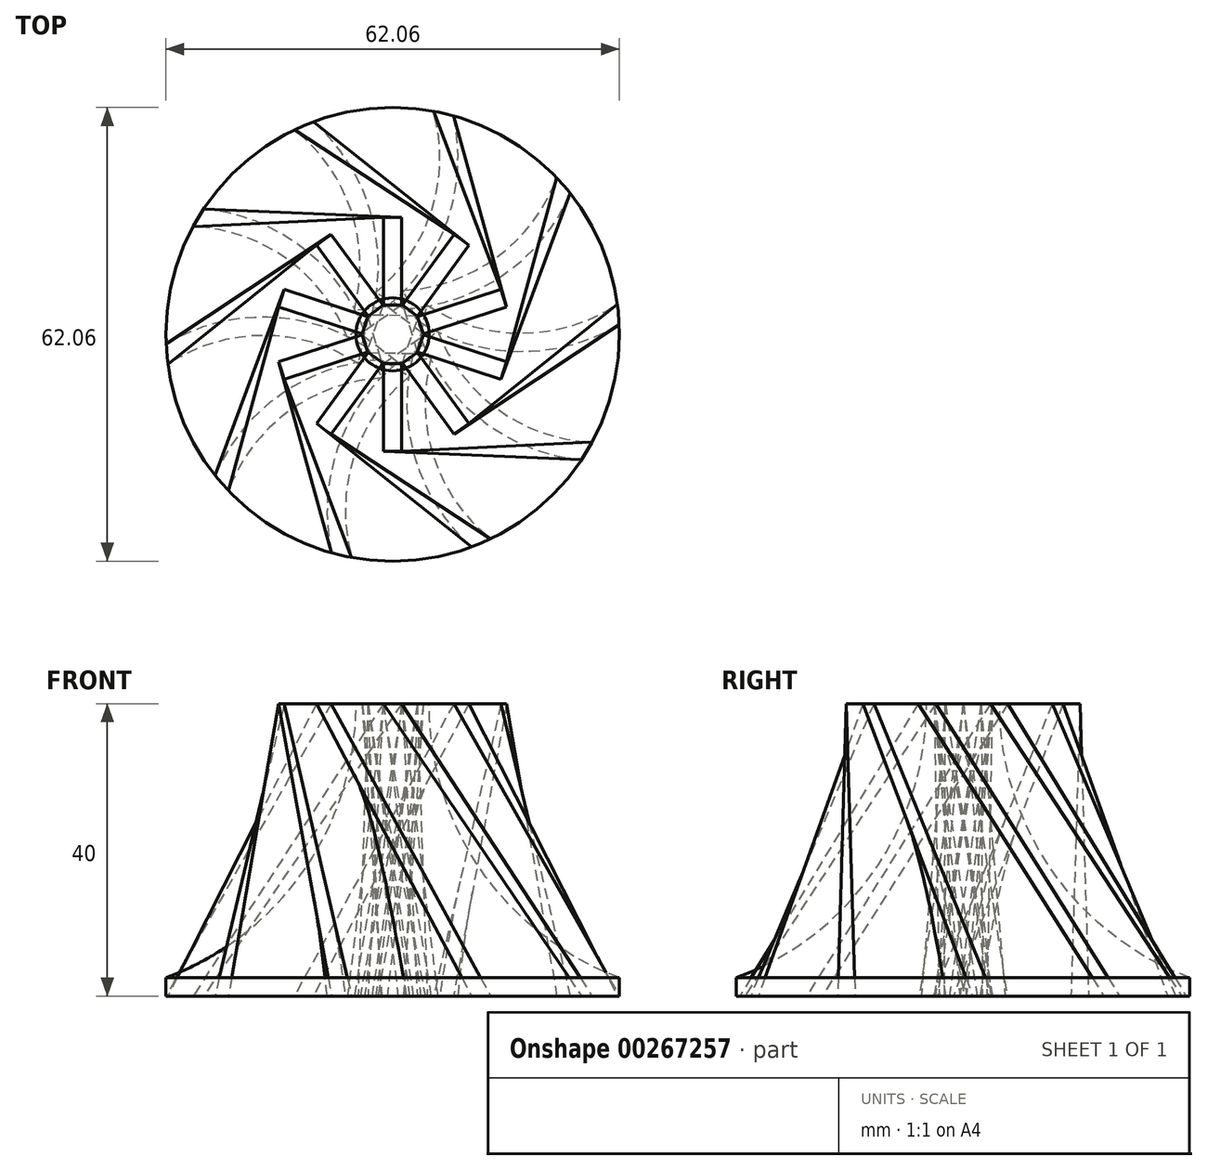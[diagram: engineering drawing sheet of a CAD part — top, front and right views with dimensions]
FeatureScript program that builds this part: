
annotation { "Feature Type Name" : "Feature", "Feature Type Description" : "" }
export const myFeature = defineFeature(function(context is Context, id is Id, definition is map)
    precondition{}
    {
        {
            var Q0;
            Q0=qCreatedBy(makeId("Front.planeOp"),FACE);
            var sketch = newSketch(context, id + "F0", { "sketchPlane" : qUnion([Q0])});
            skLineSegment(sketch, "E0", {"start": v(0, 0) * mm, "end": v(0, 40) * mm});
            skLineSegment(sketch, "E1", {"start": v(0, 40) * mm, "end": v(5, 40) * mm});
            skLineSegment(sketch, "E2", {"start": v(0, 0) * mm, "end": v(31.03, 0) * mm});
            skLineSegment(sketch, "E3", {"start": v(31.03, 0) * mm, "end": v(31.03, 2.5) * mm});
            skArc(sketch, "E4", {"start": v(5, 40) * mm, "mid": v(12.14, 17.17) * mm, "end": v(31.03, 2.5) * mm});
            skSolve(sketch);
        }
        {
            var Q0;
            Q0 = qSketchRegion(id + "F0", true);
            var Q1;
            Q1=sQuery(id+"F0.wireOp",EDGE,"E0");
            revolve(context, id + "F1", {"entities" : qUnion([Q0]), "axis" : qUnion([Q1]), "revolveType" : RevolveType.FULL});
        }
        {
            var Q0;
            Q0=makeQuery(id+"F1.opRevolve","SWEPT_FACE",FACE,{"disambiguationData":[OSD([sQuery(id+"F0.wireOp",EDGE,"E1")])]});
            cPlane(context, id + "F2", {"entities" : qUnion([Q0]), "cplaneType" : CPlaneType.OFFSET, "offset" : 0 * mm, "width" : 150 * mm, "height" : 150 * mm});
        }
        {
            var Q0;
            Q0=qCreatedBy(id+"F2.planeOp",FACE);
            var sketch = newSketch(context, id + "F3", { "sketchPlane" : qUnion([Q0])});
            skLineSegment(sketch, "E5", {"start": v(0, 0) * mm, "end": v(0, -31.03) * mm, "construction": true});
            skLineSegment(sketch, "E6.bottom", {"start": v(-1.25, -4) * mm, "end": v(1.25, -4) * mm});
            skLineSegment(sketch, "E6.top", {"start": v(-1.25, -16) * mm, "end": v(1.25, -16) * mm});
            skLineSegment(sketch, "E6.left", {"start": v(-1.25, -4) * mm, "end": v(-1.25, -16) * mm});
            skLineSegment(sketch, "E6.right", {"start": v(1.25, -4) * mm, "end": v(1.25, -16) * mm});
            skPoint(sketch, "E7", {"position": v(0, -5) * mm});
            skLineSegment(sketch, "E8", {"start": v(-5.78, -5) * mm, "end": v(5.78, -5) * mm, "construction": true});
            skSolve(sketch);
        }
        {
            var Q0;
            Q0=qCreatedBy(makeId("Front.planeOp"),FACE);
            var sketch = newSketch(context, id + "F4", { "sketchPlane" : qUnion([Q0])});
            skLineSegment(sketch, "E9", {"start": v(0, 40) * mm, "end": v(0, 0) * mm, "construction": true});
            skSolve(sketch);
        }
        {
            var Q0;
            Q0=qCreatedBy(makeId("Top.planeOp"),FACE);
            var sketch = newSketch(context, id + "F5", { "sketchPlane" : qUnion([Q0])});
            skArc(sketch, "E10", {"start": v(5, 0) * mm, "mid": v(13.47, -11.13) * mm, "end": v(26.6, -15.97) * mm, "construction": true});
            skArc(sketch, "E11.0", {"start": v(6.17, 0.45) * mm, "mid": v(14.46, -10.3) * mm, "end": v(27.3, -14.75) * mm});
            skArc(sketch, "E12.0", {"start": v(3.83, -0.45) * mm, "mid": v(12.46, -11.94) * mm, "end": v(25.85, -17.16) * mm});
            skArc(sketch, "E13.0", {"start": v(25.85, -17.16) * mm, "mid": v(26.6, -15.97) * mm, "end": v(27.3, -14.75) * mm});
            skLineSegment(sketch, "E14", {"start": v(3.83, -0.45) * mm, "end": v(6.17, 0.45) * mm});
            skSolve(sketch);
        }
        {
            var Q1;
            Q1=makeQuery(id+"F3.imprint","IMPRINT",FACE,{"disambiguationData":[TD([[makeQuery(id+"F3.imprint","IMPRINT",EDGE,{"derivedFrom":sQuery(id+"F3.wireOp",EDGE,"E6.bottom")}),-1.0]])]});
            var Q2;
            Q2=makeQuery(id+"F5.imprint","IMPRINT",FACE,{"disambiguationData":[TD([[makeQuery(id+"F5.imprint","IMPRINT",EDGE,{"derivedFrom":sQuery(id+"F5.wireOp",EDGE,"E11.0")}),-1.0]])]});
            loft(context, id + "F6", {"sheetProfilesArray" : [{ "sheetProfileEntities" : qUnion([Q1]) }, { "sheetProfileEntities" : qUnion([Q2]) }]});
        }
        {
            var Q0;
            Q0=makeQuery(id+"F6.opLoft","SWEPT_BODY",BODY,{"disambiguationData":[OSD([makeQuery(id+"F3.imprint","IMPRINT",FACE,{"disambiguationData":[TD([[makeQuery(id+"F3.imprint","IMPRINT",EDGE,{"derivedFrom":sQuery(id+"F3.wireOp",EDGE,"E6.bottom")}),-1.0]])]}),makeQuery(id+"F5.imprint","IMPRINT",FACE,{"disambiguationData":[TD([[makeQuery(id+"F5.imprint","IMPRINT",EDGE,{"derivedFrom":sQuery(id+"F5.wireOp",EDGE,"E11.0")}),-1.0]])]})])]});
            var Q1;
            Q1=sQuery(id+"F4.wireOp",EDGE,"E9");
            circularPattern(context, id + "F7", {"entities" : qUnion([Q0]), "axis" : qUnion([Q1]), "angle" : 360 * degree, "instanceCount" : 10, "equalSpace" : true});
        }
    });
